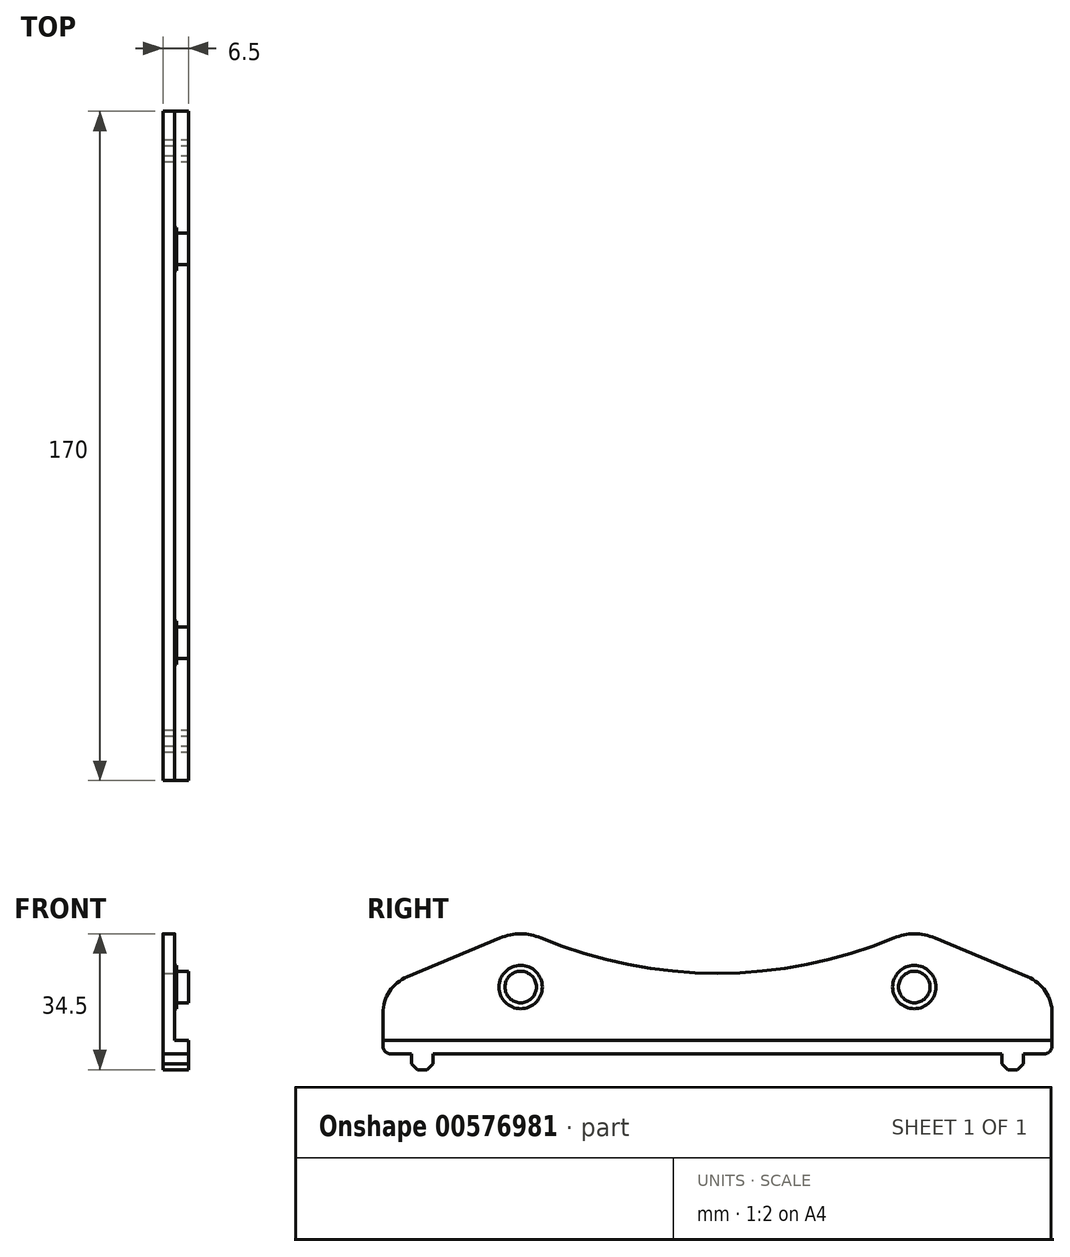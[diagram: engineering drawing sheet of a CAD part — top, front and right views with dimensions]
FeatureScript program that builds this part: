
annotation { "Feature Type Name" : "Feature", "Feature Type Description" : "" }
export const myFeature = defineFeature(function(context is Context, id is Id, definition is map)
    precondition{}
    {
        {
            var Q0;
            Q0=qCreatedBy(makeId("Right.planeOp"),FACE);
            var sketch = newSketch(context, id + "F0", { "sketchPlane" : qUnion([Q0])});
            skLineSegment(sketch, "E0", {"start": v(-85, 10.34) * mm, "end": v(-85, 0) * mm});
            skLineSegment(sketch, "E1", {"start": v(-85, 0) * mm, "end": v(85, 0) * mm});
            skLineSegment(sketch, "E2", {"start": v(85, 0) * mm, "end": v(85, 10.34) * mm});
            skCircle(sketch, "E3", {"center": v(-50, 17) * mm, "radius": 4 * mm, "construction": true});
            skCircle(sketch, "E4", {"center": v(50, 17) * mm, "radius": 4 * mm, "construction": true});
            skLineSegment(sketch, "E5", {"start": v(-50, 17) * mm, "end": v(50, 17) * mm, "construction": true});
            skPoint(sketch, "E6", {"position": v(0, 17) * mm});
            skLineSegment(sketch, "E7", {"start": v(-78.86, 19.57) * mm, "end": v(-55.2, 29.46) * mm});
            skArc(sketch, "E8", {"start": v(-44.8, 29.46) * mm, "mid": v(-50, 30.5) * mm, "end": v(-55.2, 29.46) * mm});
            skArc(sketch, "E9", {"start": v(-44.8, 29.46) * mm, "mid": v(0, 20.47) * mm, "end": v(44.8, 29.46) * mm});
            skArc(sketch, "E10", {"start": v(55.2, 29.46) * mm, "mid": v(50, 30.5) * mm, "end": v(44.8, 29.46) * mm});
            skLineSegment(sketch, "E11", {"start": v(55.2, 29.46) * mm, "end": v(78.86, 19.57) * mm});
            skPoint(sketch, "E12.visualSharp", {"position": v(-85, 17) * mm});
            skArc(sketch, "E12.filletArc", {"start": v(-78.86, 19.57) * mm, "mid": v(-83.32, 15.88) * mm, "end": v(-85, 10.34) * mm});
            skPoint(sketch, "E13.visualSharp", {"position": v(85, 17) * mm});
            skArc(sketch, "E13.filletArc", {"start": v(85, 10.34) * mm, "mid": v(83.32, 15.88) * mm, "end": v(78.86, 19.57) * mm});
            skCircle(sketch, "E14", {"center": v(-50, 17) * mm, "radius": 5.5 * mm, "construction": true});
            skCircle(sketch, "E15", {"center": v(50, 17) * mm, "radius": 5.5 * mm, "construction": true});
            skLineSegment(sketch, "E16", {"start": v(-85, 3.5) * mm, "end": v(85, 3.5) * mm, "construction": true});
            skLineSegment(sketch, "E17", {"start": v(-77.75, 0) * mm, "end": v(-77.75, -2.5) * mm});
            skLineSegment(sketch, "E18", {"start": v(-77.75, -2.5) * mm, "end": v(-76.25, -4) * mm});
            skLineSegment(sketch, "E19", {"start": v(-76.25, -4) * mm, "end": v(-73.75, -4) * mm});
            skLineSegment(sketch, "E20", {"start": v(-73.75, -4) * mm, "end": v(-72.25, -2.5) * mm});
            skLineSegment(sketch, "E21", {"start": v(-72.25, -2.5) * mm, "end": v(-72.25, 0) * mm});
            skLineSegment(sketch, "E22", {"start": v(72.25, 0) * mm, "end": v(72.25, -2.5) * mm});
            skLineSegment(sketch, "E23", {"start": v(72.25, -2.5) * mm, "end": v(73.75, -4) * mm});
            skLineSegment(sketch, "E24", {"start": v(73.75, -4) * mm, "end": v(76.25, -4) * mm});
            skLineSegment(sketch, "E25", {"start": v(76.25, -4) * mm, "end": v(77.75, -2.5) * mm});
            skLineSegment(sketch, "E26", {"start": v(77.75, -2.5) * mm, "end": v(77.75, 0) * mm});
            skLineSegment(sketch, "E27", {"start": v(-72.25, -2.5) * mm, "end": v(72.25, -2.5) * mm, "construction": true});
            skPoint(sketch, "E28", {"position": v(0, -2.5) * mm});
            skPoint(sketch, "E29", {"position": v(75, -4) * mm});
            skPoint(sketch, "E30", {"position": v(-75, -4) * mm});
            skSolve(sketch);
        }
        {
            var Q0;
            Q0 = qSketchRegion(id + "F0", true);
            extrude(context, id + "F1", {"entities" : qUnion([Q0]), "oppositeDirection" : true, "depth" : 3 * mm, "offsetDistance" : 25 * mm});
        }
        {
            var Q0;
            Q0=makeQuery(id+"F0.imprint","IMPRINT",FACE,{"disambiguationData":[TD([[makeQuery(id+"F0.imprint","IMPRINT",EDGE,{"derivedFrom":sQuery(id+"F0.wireOp",EDGE,"E0")}),1.0]])]});
            var sketch = newSketch(context, id + "F2", { "sketchPlane" : qUnion([Q0])});
            skLineSegment(sketch, "E31.2", {"start": v(-85, 3.5) * mm, "end": v(85, 3.5) * mm});
            skLineSegment(sketch, "E31.3", {"start": v(-85, 0) * mm, "end": v(85, 0) * mm});
            skLineSegment(sketch, "E31.4", {"start": v(-85, 10.34) * mm, "end": v(-85, 0) * mm});
            skLineSegment(sketch, "E31.5", {"start": v(85, 0) * mm, "end": v(85, 10.34) * mm});
            skCircle(sketch, "E32.0", {"center": v(-50, 17) * mm, "radius": 4 * mm});
            skCircle(sketch, "E32.1", {"center": v(50, 17) * mm, "radius": 4 * mm});
            skSolve(sketch);
        }
        {
            var Q0;
            Q0 = qSketchRegion(id + "F2", true);
            var Q1;
            {var subQ0=sQuery(id+"F0.wireOp",EDGE,"E17");Q1=makeQuery(id+"F0.imprint","IMPRINT",FACE,{"disambiguationData":[TD([[makeQuery(id+"F0.imprint","IMPRINT",EDGE,{"derivedFrom":subQ0}),1.0]])]});}
            var Q2;
            {var subQ0=sQuery(id+"F0.wireOp",EDGE,"E22");Q2=makeQuery(id+"F0.imprint","IMPRINT",FACE,{"disambiguationData":[TD([[makeQuery(id+"F0.imprint","IMPRINT",EDGE,{"derivedFrom":subQ0}),1.0]])]});}
            extrude(context, id + "F3", {"entities" : qUnion([Q0, Q1, Q2]), "operationType" : NewBodyOperationType.ADD, "depth" : 3.5 * mm, "offsetDistance" : 25 * mm});
        }
        {
            var Q0;
            Q0=qCreatedBy(makeId("Right.planeOp"),FACE);
            var sketch = newSketch(context, id + "F4", { "sketchPlane" : qUnion([Q0])});
            skCircle(sketch, "E33.0", {"center": v(-50, 17) * mm, "radius": 4 * mm});
            skCircle(sketch, "E33.1", {"center": v(-50, 17) * mm, "radius": 5.5 * mm});
            skCircle(sketch, "E33.2", {"center": v(50, 17) * mm, "radius": 4 * mm});
            skCircle(sketch, "E33.3", {"center": v(50, 17) * mm, "radius": 5.5 * mm});
            skSolve(sketch);
        }
        {
            var Q0;
            Q0 = qSketchRegion(id + "F4", true);
            extrude(context, id + "F5", {"entities" : qUnion([Q0]), "operationType" : NewBodyOperationType.ADD, "depth" : 0.5 * mm, "offsetDistance" : 25 * mm});
        }
        {
            var Q0;
            Q0=makeQuery(id+"F3.boolean.opBoolean","MERGE",EDGE,{"derivedFrom":[makeQuery(id+"F1.opExtrude","SWEPT_EDGE",EDGE,{"disambiguationData":[OSD([sQuery(id+"F0.wireOp",EDGE,"E0"),sQuery(id+"F0.wireOp",EDGE,"E1")])]}),makeQuery(id+"F3.opExtrude","SWEPT_EDGE",EDGE,{"disambiguationData":[OSD([sQuery(id+"F2.wireOp",EDGE,"E31.3"),sQuery(id+"F2.wireOp",EDGE,"E31.4")])]})]});
            var Q1;
            Q1=makeQuery(id+"F3.boolean.opBoolean","MERGE",EDGE,{"derivedFrom":[makeQuery(id+"F1.opExtrude","SWEPT_EDGE",EDGE,{"disambiguationData":[OSD([sQuery(id+"F0.wireOp",EDGE,"E1"),sQuery(id+"F0.wireOp",EDGE,"E2")])]}),makeQuery(id+"F3.opExtrude","SWEPT_EDGE",EDGE,{"disambiguationData":[OSD([sQuery(id+"F2.wireOp",EDGE,"E31.3"),sQuery(id+"F2.wireOp",EDGE,"E31.5")])]})]});
            fillet(context, id + "F6", {"entities" : qUnion([Q0, Q1]), "radius" : 2 * mm, "tangentPropagation" : true, "allowEdgeOverflow" : false});
        }
    });
